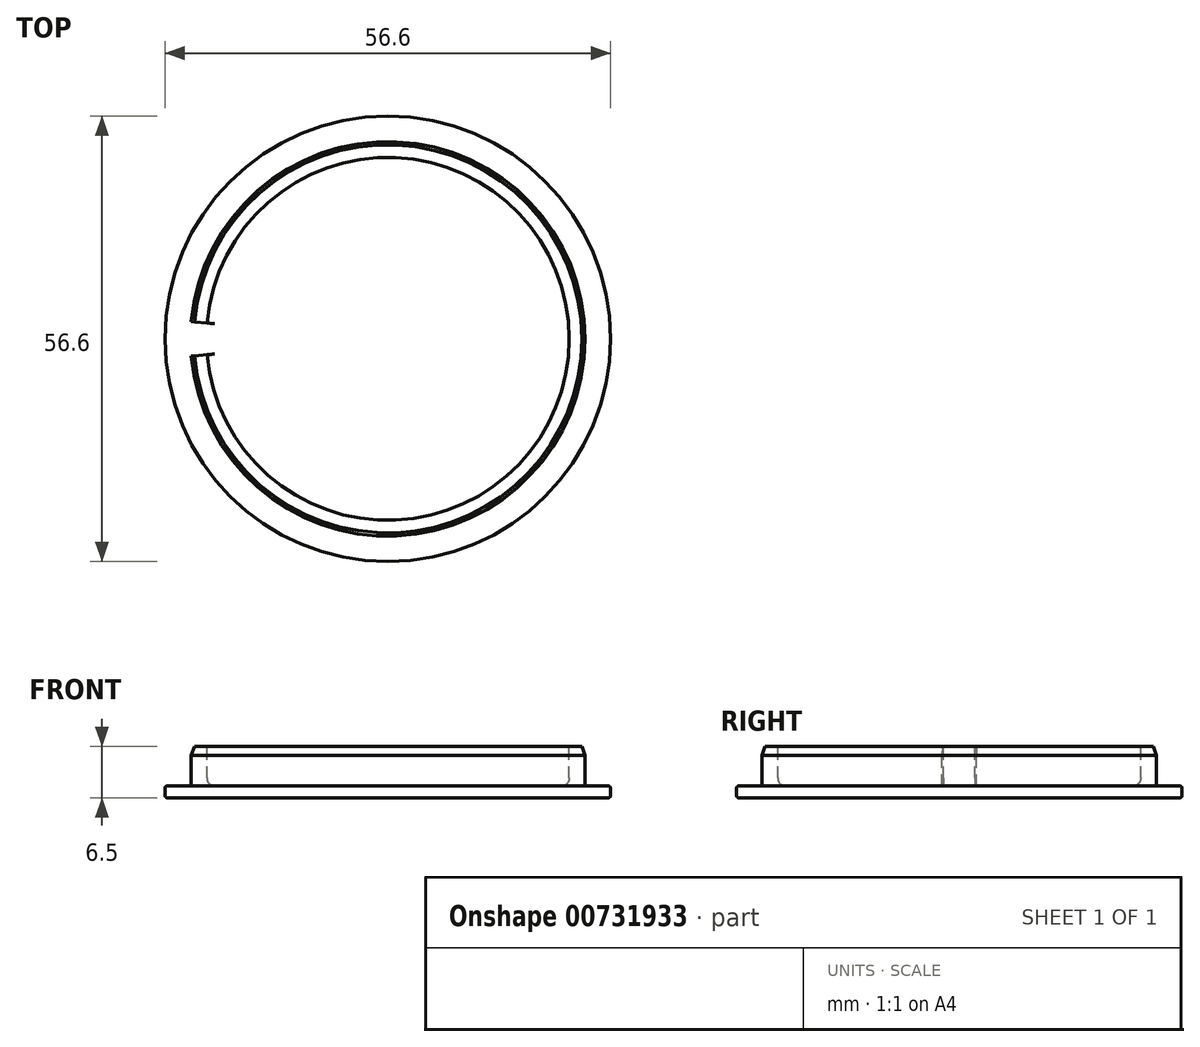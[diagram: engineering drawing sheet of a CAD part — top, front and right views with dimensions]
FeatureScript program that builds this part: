
annotation { "Feature Type Name" : "Feature", "Feature Type Description" : "" }
export const myFeature = defineFeature(function(context is Context, id is Id, definition is map)
    precondition{}
    {
        {
            var Q0;
            Q0=qCreatedBy(makeId("Front.planeOp"),FACE);
            var sketch = newSketch(context, id + "F0", { "sketchPlane" : qUnion([Q0])});
            skLineSegment(sketch, "E0", {"start": v(0, 0) * mm, "end": v(-28.3, 0) * mm});
            skLineSegment(sketch, "E1", {"start": v(-28.3, 0) * mm, "end": v(-28.3, 1.5) * mm});
            skLineSegment(sketch, "E2", {"start": v(-28.3, 1.5) * mm, "end": v(-25.05, 1.5) * mm});
            skLineSegment(sketch, "E3", {"start": v(-25.05, 1.5) * mm, "end": v(-25.05, 6.5) * mm});
            skLineSegment(sketch, "E4", {"start": v(-25.05, 6.5) * mm, "end": v(-23.05, 6.5) * mm});
            skLineSegment(sketch, "E5", {"start": v(-23.05, 6.5) * mm, "end": v(-23.05, 1.5) * mm});
            skLineSegment(sketch, "E6", {"start": v(-23.05, 1.5) * mm, "end": v(0, 1.5) * mm});
            skLineSegment(sketch, "E7", {"start": v(0, 70.02) * mm, "end": v(0, -71.1) * mm, "construction": true});
            skLineSegment(sketch, "E8", {"start": v(0, 1.5) * mm, "end": v(0, 0) * mm});
            skSolve(sketch);
        }
        {
            var Q0;
            Q0 = qSketchRegion(id + "F0", true);
            var Q1;
            Q1=sQuery(id+"F0.wireOp",EDGE,"E7");
            revolve(context, id + "F1", {"surfaceOperationType" : NewSurfaceOperationType.NEW, "entities" : qUnion([Q0]), "axis" : qUnion([Q1]), "revolveType" : RevolveType.FULL});
        }
        {
            var Q0;
            Q0=makeQuery(id+"F1.opRevolve","SWEPT_EDGE",EDGE,{"disambiguationData":[OSD([sQuery(id+"F0.wireOp",EDGE,"E3"),sQuery(id+"F0.wireOp",EDGE,"E4")])]});
            chamfer(context, id + "F2", {"entities" : qUnion([Q0]), "chamferType" : ChamferType.OFFSET_ANGLE, "width" : 0.4 * mm, "oppositeDirection" : false, "angle" : 70 * degree, "tangentPropagation" : true});
        }
        {
            var Q0;
            Q0=qCreatedBy(makeId("Front.planeOp"),FACE);
            var sketch = newSketch(context, id + "F3", { "sketchPlane" : qUnion([Q0])});
            skLineSegment(sketch, "E9.0", {"start": v(-28.3, 1.5) * mm, "end": v(28.3, 1.5) * mm, "construction": true});
            skLineSegment(sketch, "E10.bottom", {"start": v(-25.89, 1.5) * mm, "end": v(-18.57, 1.5) * mm});
            skLineSegment(sketch, "E10.top", {"start": v(-25.89, 7.62) * mm, "end": v(-18.57, 7.62) * mm});
            skLineSegment(sketch, "E10.left", {"start": v(-25.89, 1.5) * mm, "end": v(-25.89, 7.62) * mm});
            skLineSegment(sketch, "E10.right", {"start": v(-18.57, 1.5) * mm, "end": v(-18.57, 7.62) * mm});
            skLineSegment(sketch, "E11", {"start": v(0, 38.02) * mm, "end": v(0, -23.91) * mm, "construction": true});
            skSolve(sketch);
        }
        {
            var Q0;
            Q0=makeQuery(id+"F1.opRevolve","SWEPT_EDGE",EDGE,{"disambiguationData":[OSD([sQuery(id+"F0.wireOp",EDGE,"E5"),sQuery(id+"F0.wireOp",EDGE,"E6")])]});
            fillet(context, id + "F4", {"entities" : qUnion([Q0]), "radius" : 1 * mm, "tangentPropagation" : true, "allowEdgeOverflow" : false});
        }
        {
            var Q0;
            Q0 = qSketchRegion(id + "F3", true);
            var Q1;
            Q1=sQuery(id+"F3.wireOp",EDGE,"E11");
            revolve(context, id + "F5", {"operationType" : NewBodyOperationType.REMOVE, "surfaceOperationType" : NewSurfaceOperationType.NEW, "entities" : qUnion([Q0]), "axis" : qUnion([Q1]), "revolveType" : RevolveType.SYMMETRIC, "oppositeDirection" : true, "angle" : 10 * degree});
        }
        {
            var Q0;
            Q0=makeQuery(id+"F1.opRevolve","SWEPT_EDGE",EDGE,{"disambiguationData":[OSD([sQuery(id+"F0.wireOp",EDGE,"E1"),sQuery(id+"F0.wireOp",EDGE,"E2")])]});
            var Q1;
            Q1=makeQuery(id+"F1.opRevolve","SWEPT_EDGE",EDGE,{"disambiguationData":[OSD([sQuery(id+"F0.wireOp",EDGE,"E0"),sQuery(id+"F0.wireOp",EDGE,"E1")])]});
            fillet(context, id + "F6", {"entities" : qUnion([Q0, Q1]), "radius" : 0.3 * mm, "tangentPropagation" : true, "allowEdgeOverflow" : false});
        }
    });
